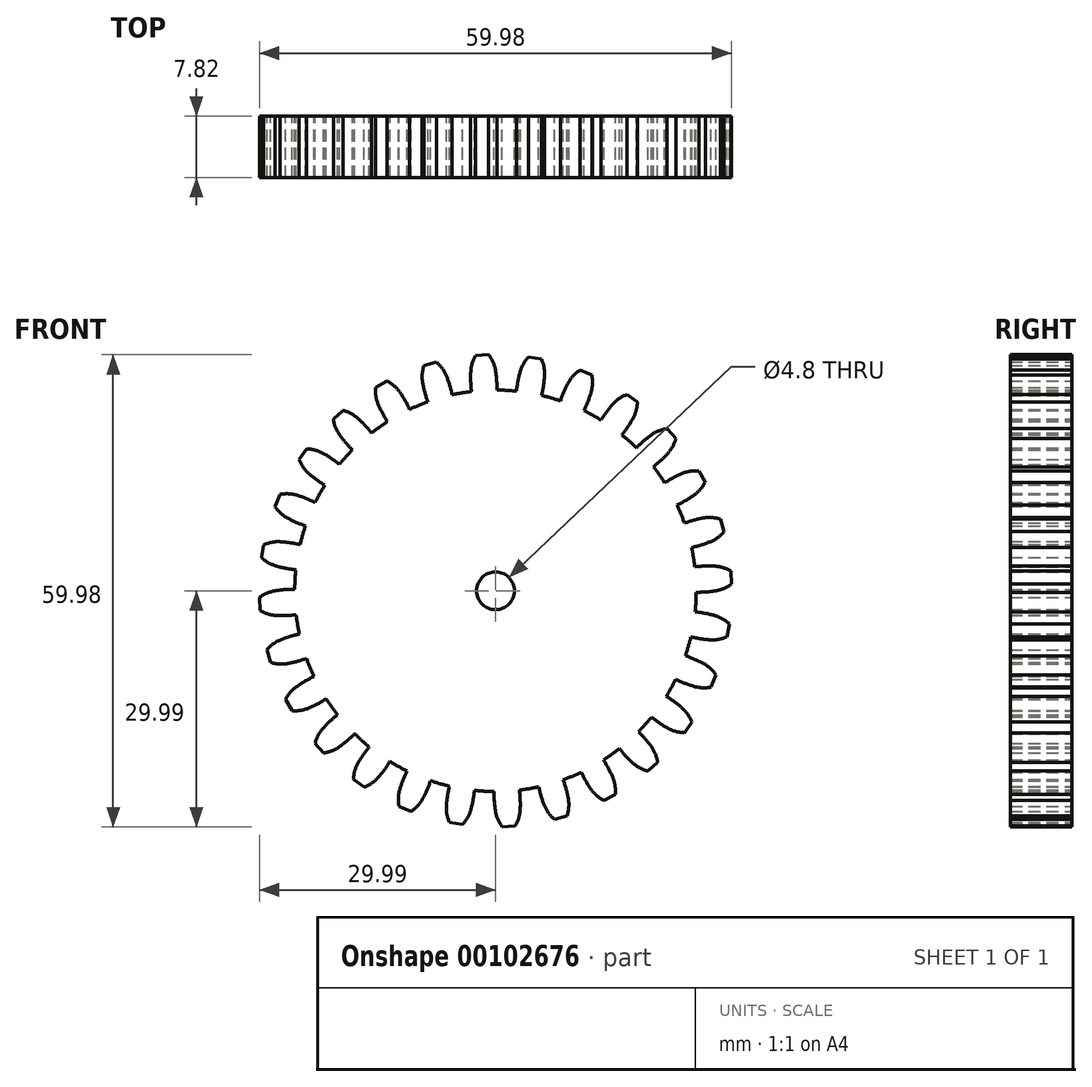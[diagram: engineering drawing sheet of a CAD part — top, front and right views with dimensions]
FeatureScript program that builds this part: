
annotation { "Feature Type Name" : "Feature", "Feature Type Description" : "" }
export const myFeature = defineFeature(function(context is Context, id is Id, definition is map)
    precondition{}
    {
        {
            var Q0;
            Q0=qCreatedBy(makeId("Front.planeOp"),FACE);
            var sketch = newSketch(context, id + "F0", { "sketchPlane" : qUnion([Q0])});
            skCircle(sketch, "E0", {"center": v(0, 0) * mm, "radius": 30 * mm, "construction": true});
            skCircle(sketch, "E1", {"center": v(0, 0) * mm, "radius": 2.4 * mm});
            skCircle(sketch, "E2", {"center": v(0, 0) * mm, "radius": 28 * mm, "construction": true});
            skCircle(sketch, "E3", {"center": v(0, 0) * mm, "radius": 25.5 * mm});
            skLineSegment(sketch, "E4", {"start": v(0, 0) * mm, "end": v(0, 41.45) * mm, "construction": true});
            skLineSegment(sketch, "E5", {"start": v(0, 0) * mm, "end": v(-2.37, 42.16) * mm, "construction": true});
            skLineSegment(sketch, "E6", {"start": v(0, 28) * mm, "end": v(-37.7, 28) * mm, "construction": true});
            skLineSegment(sketch, "E7", {"start": v(0, 28) * mm, "end": v(-36.12, 18.66) * mm, "construction": true});
            skCircle(sketch, "E8", {"center": v(0, 0) * mm, "radius": 27.1 * mm});
            skCircle(sketch, "E9", {"center": v(0, 28) * mm, "radius": 7 * mm, "construction": true});
            skCircle(sketch, "E10", {"center": v(-6.78, 26.25) * mm, "radius": 7 * mm, "construction": true});
            skArc(sketch, "E11", {"start": v(0, 28) * mm, "mid": v(-0.3, 29.05) * mm, "end": v(-0.86, 29.99) * mm});
            skArc(sketch, "E12", {"start": v(0.18, 25.5) * mm, "mid": v(0.15, 26.75) * mm, "end": v(0, 28) * mm});
            skArc(sketch, "E13.MirrorCS", {"start": v(-3.14, 27.82) * mm, "mid": v(-2.95, 28.9) * mm, "end": v(-2.5, 29.9) * mm});
            skArc(sketch, "E14.MirrorCS", {"start": v(-3.04, 25.32) * mm, "mid": v(-3.14, 26.57) * mm, "end": v(-3.14, 27.82) * mm});
            skLineSegment(sketch, "E15", {"start": v(-2.5, 29.9) * mm, "end": v(-0.86, 29.99) * mm});
            skSolve(sketch);
        }
        {
            var Q0;
            Q0=makeQuery(id+"F0.imprint","IMPRINT",FACE,{"disambiguationData":[TD([[makeQuery(id+"F0.imprint","IMPRINT",EDGE,{"derivedFrom":sQuery(id+"F0.wireOp",EDGE,"E1")}),-1.0]])]});
            var Q1;
            {var subQ0=sQuery(id+"F0.wireOp",EDGE,"E12");var subQ1=sQuery(id+"F0.wireOp",EDGE,"E3");var subQ2=makeQuery(id+"F0.imprint","INTERSECT",VERTEX,{"derivedFrom":[subQ1,subQ0]});Q1=makeQuery(id+"F0.imprint","IMPRINT",FACE,{"disambiguationData":[TD([[makeQuery(id+"F0.imprint","IMPRINT",EDGE,{"disambiguationData":[TD([[subQ2,-1.0]])],"derivedFrom":subQ1}),-1.0]])]});}
            var Q2;
            {var subQ2=sQuery(id+"F0.wireOp",EDGE,"E11");Q2=makeQuery(id+"F0.imprint","IMPRINT",FACE,{"disambiguationData":[TD([[makeQuery(id+"F0.imprint","IMPRINT",EDGE,{"derivedFrom":subQ2}),1.0]])]});}
            extrude(context, id + "F1", {"entities" : qUnion([Q0, Q1, Q2]), "depth" : 7.82 * mm});
        }
        {
            var Q0;
            Q0=makeQuery(id+"F1.opExtrude","SWEPT_BODY",BODY,{"disambiguationData":[OSD([sQuery(id+"F0.wireOp",EDGE,"E1"),sQuery(id+"F0.wireOp",EDGE,"E3"),sQuery(id+"F0.wireOp",EDGE,"E10"),sQuery(id+"F0.wireOp",EDGE,"E11"),sQuery(id+"F0.wireOp",EDGE,"E12"),sQuery(id+"F0.wireOp",EDGE,"E13.MirrorCS"),sQuery(id+"F0.wireOp",EDGE,"E14.MirrorCS"),sQuery(id+"F0.wireOp",EDGE,"E15")])]});
            var Q1;
            Q1=makeQuery(id+"F1.opExtrude","SWEPT_FACE",FACE,{"disambiguationData":[OSD([sQuery(id+"F0.wireOp",EDGE,"E3")])]});
            circularPattern(context, id + "F2", {"operationType" : NewBodyOperationType.ADD, "entities" : qUnion([Q0]), "axis" : qUnion([Q1]), "angle" : 12.86 * degree, "instanceCount" : 28});
        }
    });
